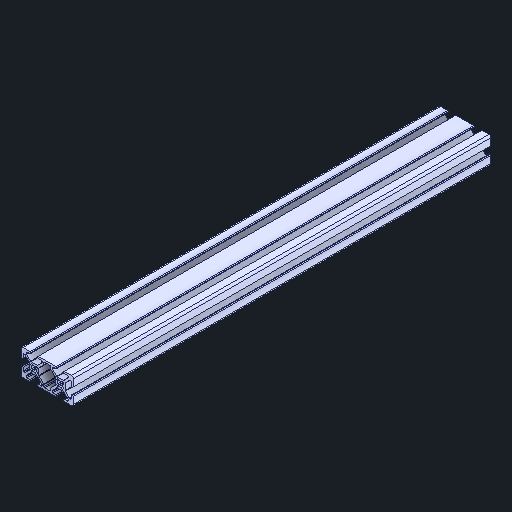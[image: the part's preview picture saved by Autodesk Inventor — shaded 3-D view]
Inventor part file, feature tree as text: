
AUTODESK INVENTOR PART (.ipt)
format: ipt  version: 2025 (Build 290162000, 162)  size: 253,952 bytes
history: native  units: in
note: dims shown in document units (in); Inventor stores cm internally (conversion verified against a paired STEP export)
features: extrude x1
ambient origin geometry x8: Origin, YZ Plane, XZ Plane, XY Plane, X Axis, Y Axis, Z Axis, Center Point
bodies: Solid1 (feature_tree)
feature tree (1):
  extrude  "Extrude1"  [1 undecoded]
note: 1 required parameter value undecoded (feature->parameter linkage not recoverable at this tier; creation-order binding heuristic only, values carry confidence <= 0.55)
